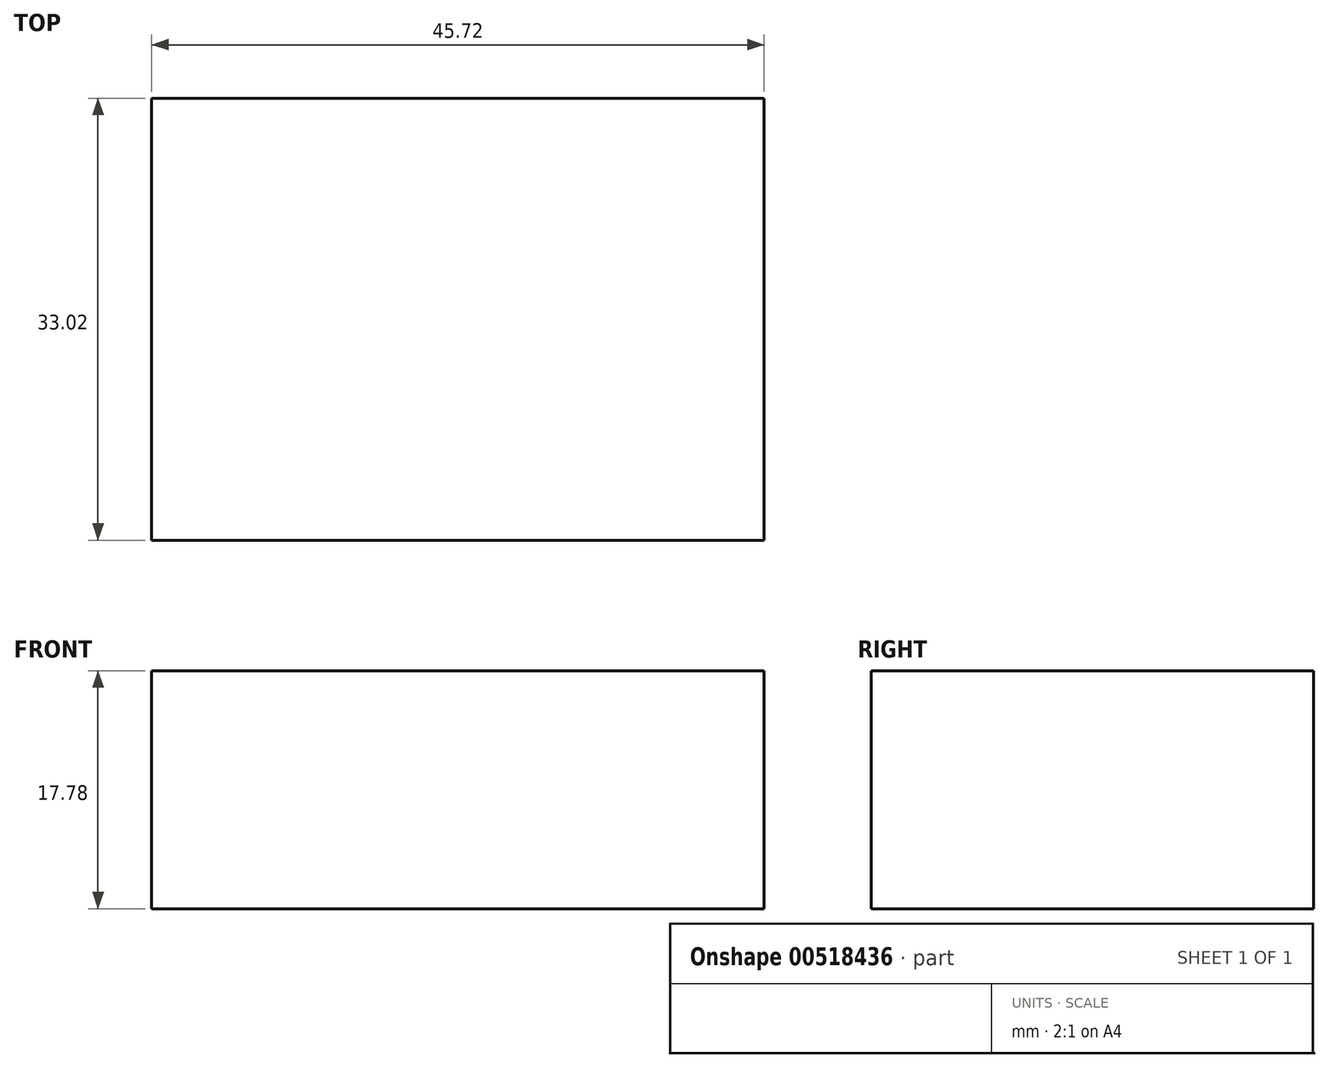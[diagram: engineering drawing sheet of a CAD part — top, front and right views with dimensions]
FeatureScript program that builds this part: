
annotation { "Feature Type Name" : "Feature", "Feature Type Description" : "" }
export const myFeature = defineFeature(function(context is Context, id is Id, definition is map)
    precondition{}
    {
        {
            var Q0;
            Q0=qCreatedBy(makeId("Top.planeOp"),FACE);
            var sketch = newSketch(context, id + "F0", { "sketchPlane" : qUnion([Q0])});
            skLineSegment(sketch, "E0.bottom", {"start": v(0, 0) * mm, "end": v(45.72, 0) * mm});
            skLineSegment(sketch, "E0.top", {"start": v(0, -33.02) * mm, "end": v(45.72, -33.02) * mm});
            skLineSegment(sketch, "E0.left", {"start": v(0, 0) * mm, "end": v(0, -33.02) * mm});
            skLineSegment(sketch, "E0.right", {"start": v(45.72, 0) * mm, "end": v(45.72, -33.02) * mm});
            skSolve(sketch);
        }
        {
            var Q0;
            Q0=makeQuery(id+"F0.imprint","IMPRINT",FACE,{"disambiguationData":[TD([[makeQuery(id+"F0.imprint","IMPRINT",EDGE,{"derivedFrom":sQuery(id+"F0.wireOp",EDGE,"E0.bottom")}),-1.0]])]});
            extrude(context, id + "F1", {"entities" : qUnion([Q0]), "depth" : 17.78 * mm, "offsetDistance" : 25 * mm});
        }
    });
